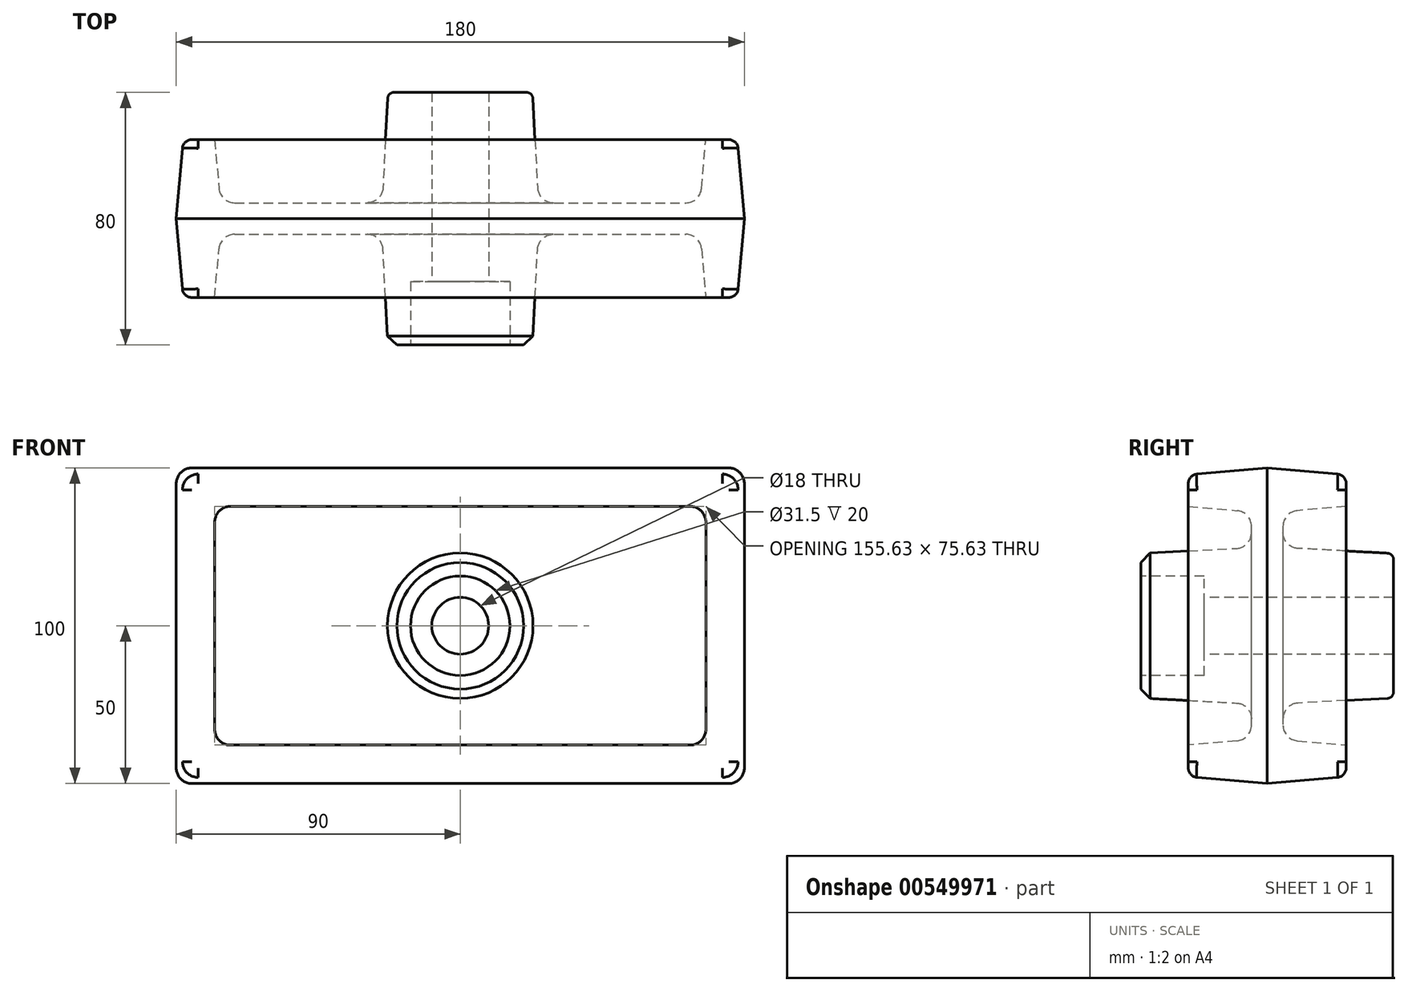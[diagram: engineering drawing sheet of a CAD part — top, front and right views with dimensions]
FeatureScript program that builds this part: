
annotation { "Feature Type Name" : "Feature", "Feature Type Description" : "" }
export const myFeature = defineFeature(function(context is Context, id is Id, definition is map)
    precondition{}
    {
        {
            var Q0;
            Q0=qCreatedBy(makeId("Front.planeOp"),FACE);
            var sketch = newSketch(context, id + "F0", { "sketchPlane" : qUnion([Q0])});
            skLineSegment(sketch, "E0.bottom", {"start": v(90, -50) * mm, "end": v(-90, -50) * mm});
            skLineSegment(sketch, "E0.top", {"start": v(90, 50) * mm, "end": v(-90, 50) * mm});
            skLineSegment(sketch, "E0.left", {"start": v(90, -50) * mm, "end": v(90, 50) * mm});
            skLineSegment(sketch, "E0.right", {"start": v(-90, -50) * mm, "end": v(-90, 50) * mm});
            skPoint(sketch, "E0.middle", {"position": v(0, 0) * mm});
            skSolve(sketch);
        }
        {
            var Q0;
            Q0 = qSketchRegion(id + "F0", true);
            extrude(context, id + "F1", {"entities" : qUnion([Q0]), "depth" : 25 * mm, "offsetDistance" : 25 * mm, "hasDraft" : true, "draftAngle" : 5 * degree, "draftPullDirection" : true, "hasSecondDirection" : true, "secondDirectionOppositeDirection" : true, "secondDirectionDepth" : 25 * mm, "hasSecondDirectionDraft" : true, "secondDirectionDraftAngle" : 5 * degree, "secondDirectionDraftPullDirection" : true});
        }
        {
            var Q0;
            Q0=makeQuery(id+"F1.opExtrude","CAP_FACE",FACE,{"disambiguationData":[OSD([sQuery(id+"F0.wireOp",EDGE,"E0.bottom"),sQuery(id+"F0.wireOp",EDGE,"E0.top"),sQuery(id+"F0.wireOp",EDGE,"E0.left"),sQuery(id+"F0.wireOp",EDGE,"E0.right")])],"isStart":false});
            var sketch = newSketch(context, id + "F2", { "sketchPlane" : qUnion([Q0])});
            skLineSegment(sketch, "E1.0", {"start": v(77.81, -37.81) * mm, "end": v(-77.81, -37.81) * mm});
            skLineSegment(sketch, "E1.1", {"start": v(77.81, -37.81) * mm, "end": v(77.81, 37.81) * mm});
            skLineSegment(sketch, "E1.2", {"start": v(77.81, 37.81) * mm, "end": v(-77.81, 37.81) * mm});
            skLineSegment(sketch, "E1.3", {"start": v(-77.81, -37.81) * mm, "end": v(-77.81, 37.81) * mm});
            skSolve(sketch);
        }
        {
            var Q0;
            Q0 = qSketchRegion(id + "F2", true);
            extrude(context, id + "F3", {"entities" : qUnion([Q0]), "operationType" : NewBodyOperationType.REMOVE, "oppositeDirection" : true, "depth" : 20 * mm, "offsetDistance" : 25 * mm, "hasDraft" : true, "draftAngle" : 5 * degree, "draftPullDirection" : true});
        }
        {
            var Q0;
            Q0=makeQuery(id+"F1.opExtrude","CAP_FACE",FACE,{"disambiguationData":[OSD([sQuery(id+"F0.wireOp",EDGE,"E0.bottom"),sQuery(id+"F0.wireOp",EDGE,"E0.top"),sQuery(id+"F0.wireOp",EDGE,"E0.left"),sQuery(id+"F0.wireOp",EDGE,"E0.right")])],"isStart":true});
            var sketch = newSketch(context, id + "F4", { "sketchPlane" : qUnion([Q0])});
            skLineSegment(sketch, "E2.0", {"start": v(-77.81, 37.81) * mm, "end": v(77.81, 37.81) * mm});
            skLineSegment(sketch, "E2.1", {"start": v(-77.81, -37.81) * mm, "end": v(-77.81, 37.81) * mm});
            skLineSegment(sketch, "E2.2", {"start": v(-77.81, -37.81) * mm, "end": v(77.81, -37.81) * mm});
            skLineSegment(sketch, "E2.3", {"start": v(77.81, -37.81) * mm, "end": v(77.81, 37.81) * mm});
            skSolve(sketch);
        }
        {
            var Q0;
            Q0 = qSketchRegion(id + "F4", true);
            extrude(context, id + "F5", {"entities" : qUnion([Q0]), "operationType" : NewBodyOperationType.REMOVE, "oppositeDirection" : true, "depth" : 20 * mm, "offsetDistance" : 25 * mm, "hasDraft" : true, "draftAngle" : 5 * degree, "draftPullDirection" : true});
        }
        {
            var Q0;
            Q0=makeQuery(id+"F5.boolean.opBoolean","COPY",EDGE,{"derivedFrom":makeQuery(id+"F5.opExtrude","SWEPT_EDGE",EDGE,{"disambiguationData":[OSD([sQuery(id+"F4.wireOp",EDGE,"E2.1"),sQuery(id+"F4.wireOp",EDGE,"E2.2")])]})});
            var Q1;
            Q1=makeQuery(id+"F3.boolean.opBoolean","COPY",EDGE,{"derivedFrom":makeQuery(id+"F3.opExtrude","SWEPT_EDGE",EDGE,{"disambiguationData":[OSD([sQuery(id+"F2.wireOp",EDGE,"E1.0"),sQuery(id+"F2.wireOp",EDGE,"E1.1")])]})});
            var Q2;
            Q2=makeQuery(id+"F3.boolean.opBoolean","COPY",EDGE,{"derivedFrom":makeQuery(id+"F3.opExtrude","SWEPT_EDGE",EDGE,{"disambiguationData":[OSD([sQuery(id+"F2.wireOp",EDGE,"E1.2"),sQuery(id+"F2.wireOp",EDGE,"E1.3")])]})});
            var Q3;
            Q3=makeQuery(id+"F5.boolean.opBoolean","COPY",EDGE,{"derivedFrom":makeQuery(id+"F5.opExtrude","SWEPT_EDGE",EDGE,{"disambiguationData":[OSD([sQuery(id+"F4.wireOp",EDGE,"E2.2"),sQuery(id+"F4.wireOp",EDGE,"E2.3")])]})});
            var Q4;
            Q4=makeQuery(id+"F5.boolean.opBoolean","COPY",EDGE,{"derivedFrom":makeQuery(id+"F5.opExtrude","SWEPT_EDGE",EDGE,{"disambiguationData":[OSD([sQuery(id+"F4.wireOp",EDGE,"E2.0"),sQuery(id+"F4.wireOp",EDGE,"E2.3")])]})});
            var Q5;
            Q5=makeQuery(id+"F5.boolean.opBoolean","COPY",EDGE,{"derivedFrom":makeQuery(id+"F5.opExtrude","SWEPT_EDGE",EDGE,{"disambiguationData":[OSD([sQuery(id+"F4.wireOp",EDGE,"E2.0"),sQuery(id+"F4.wireOp",EDGE,"E2.1")])]})});
            var Q6;
            Q6=makeQuery(id+"F3.boolean.opBoolean","COPY",EDGE,{"derivedFrom":makeQuery(id+"F3.opExtrude","SWEPT_EDGE",EDGE,{"disambiguationData":[OSD([sQuery(id+"F2.wireOp",EDGE,"E1.0"),sQuery(id+"F2.wireOp",EDGE,"E1.3")])]})});
            var Q7;
            Q7=makeQuery(id+"F3.boolean.opBoolean","COPY",EDGE,{"derivedFrom":makeQuery(id+"F3.opExtrude","SWEPT_EDGE",EDGE,{"disambiguationData":[OSD([sQuery(id+"F2.wireOp",EDGE,"E1.1"),sQuery(id+"F2.wireOp",EDGE,"E1.2")])]})});
            fillet(context, id + "F6", {"entities" : qUnion([Q0, Q1, Q2, Q3, Q4, Q5, Q6, Q7]), "radius" : 5 * mm, "allowEdgeOverflow" : false});
        }
        {
            var Q0;
            Q0=makeQuery(id+"F3.boolean.opBoolean","COPY",EDGE,{"derivedFrom":makeQuery(id+"F3.opExtrude","CAP_EDGE",EDGE,{"disambiguationData":[OSD([sQuery(id+"F2.wireOp",EDGE,"E1.0")])],"isStart":false})});
            var Q1;
            Q1=makeQuery(id+"F5.boolean.opBoolean","COPY",EDGE,{"derivedFrom":makeQuery(id+"F5.opExtrude","CAP_EDGE",EDGE,{"disambiguationData":[OSD([sQuery(id+"F4.wireOp",EDGE,"E2.2")])],"isStart":false})});
            fillet(context, id + "F7", {"entities" : qUnion([Q0, Q1]), "radius" : 5 * mm, "tangentPropagation" : true, "allowEdgeOverflow" : false});
        }
        {
            var Q0;
            Q0=makeQuery(id+"F1.*.split.splitOp","SPLIT",EDGE,{"derivedFrom":makeQuery(id+"F1.opExtrude","SWEPT_EDGE",EDGE,{"disambiguationData":[OSD([sQuery(id+"F0.wireOp",EDGE,"E0.bottom"),sQuery(id+"F0.wireOp",EDGE,"E0.right")])]}),"isFromBackBody":true});
            var Q1;
            Q1=makeQuery(id+"F1.*.split.splitOp","SPLIT",EDGE,{"derivedFrom":makeQuery(id+"F1.opExtrude","SWEPT_EDGE",EDGE,{"disambiguationData":[OSD([sQuery(id+"F0.wireOp",EDGE,"E0.top"),sQuery(id+"F0.wireOp",EDGE,"E0.left")])]})});
            var Q2;
            Q2=makeQuery(id+"F1.*.split.splitOp","SPLIT",EDGE,{"derivedFrom":makeQuery(id+"F1.opExtrude","SWEPT_EDGE",EDGE,{"disambiguationData":[OSD([sQuery(id+"F0.wireOp",EDGE,"E0.top"),sQuery(id+"F0.wireOp",EDGE,"E0.left")])]}),"isFromBackBody":true});
            var Q3;
            Q3=makeQuery(id+"F1.*.split.splitOp","SPLIT",EDGE,{"derivedFrom":makeQuery(id+"F1.opExtrude","SWEPT_EDGE",EDGE,{"disambiguationData":[OSD([sQuery(id+"F0.wireOp",EDGE,"E0.top"),sQuery(id+"F0.wireOp",EDGE,"E0.right")])]}),"isFromBackBody":true});
            var Q4;
            Q4=makeQuery(id+"F1.*.split.splitOp","SPLIT",EDGE,{"derivedFrom":makeQuery(id+"F1.opExtrude","SWEPT_EDGE",EDGE,{"disambiguationData":[OSD([sQuery(id+"F0.wireOp",EDGE,"E0.top"),sQuery(id+"F0.wireOp",EDGE,"E0.right")])]})});
            var Q5;
            Q5=makeQuery(id+"F1.*.split.splitOp","SPLIT",EDGE,{"derivedFrom":makeQuery(id+"F1.opExtrude","SWEPT_EDGE",EDGE,{"disambiguationData":[OSD([sQuery(id+"F0.wireOp",EDGE,"E0.bottom"),sQuery(id+"F0.wireOp",EDGE,"E0.left")])]}),"isFromBackBody":true});
            var Q6;
            Q6=makeQuery(id+"F1.*.split.splitOp","SPLIT",EDGE,{"derivedFrom":makeQuery(id+"F1.opExtrude","SWEPT_EDGE",EDGE,{"disambiguationData":[OSD([sQuery(id+"F0.wireOp",EDGE,"E0.bottom"),sQuery(id+"F0.wireOp",EDGE,"E0.right")])]})});
            var Q7;
            Q7=makeQuery(id+"F1.*.split.splitOp","SPLIT",EDGE,{"derivedFrom":makeQuery(id+"F1.opExtrude","SWEPT_EDGE",EDGE,{"disambiguationData":[OSD([sQuery(id+"F0.wireOp",EDGE,"E0.bottom"),sQuery(id+"F0.wireOp",EDGE,"E0.left")])]})});
            fillet(context, id + "F8", {"entities" : qUnion([Q0, Q1, Q2, Q3, Q4, Q5, Q6, Q7]), "radius" : 5 * mm, "tangentPropagation" : true, "allowEdgeOverflow" : false});
        }
        {
            var Q0;
            Q0=makeQuery(id+"F1.opExtrude","CAP_EDGE",EDGE,{"disambiguationData":[OSD([sQuery(id+"F0.wireOp",EDGE,"E0.top")])],"isStart":false});
            var Q1;
            Q1=makeQuery(id+"F1.opExtrude","CAP_EDGE",EDGE,{"disambiguationData":[OSD([sQuery(id+"F0.wireOp",EDGE,"E0.top")])],"isStart":true});
            var Q2;
            Q2=makeQuery(id+"F5.boolean.opBoolean","COPY",EDGE,{"derivedFrom":makeQuery(id+"F5.opExtrude","CAP_EDGE",EDGE,{"disambiguationData":[OSD([sQuery(id+"F4.wireOp",EDGE,"E2.0")])],"isStart":true})});
            var Q3;
            Q3=makeQuery(id+"F3.boolean.opBoolean","COPY",EDGE,{"derivedFrom":makeQuery(id+"F3.opExtrude","CAP_EDGE",EDGE,{"disambiguationData":[OSD([sQuery(id+"F2.wireOp",EDGE,"E1.2")])],"isStart":true})});
            fillet(context, id + "F9", {"entities" : qUnion([Q0, Q1, Q2, Q3]), "radius" : 3 * mm, "tangentPropagation" : true, "allowEdgeOverflow" : false});
        }
        {
            var Q0;
            Q0=qCreatedBy(makeId("Front.planeOp"),FACE);
            var sketch = newSketch(context, id + "F10", { "sketchPlane" : qUnion([Q0])});
            skCircle(sketch, "E3", {"center": v(0, 0) * mm, "radius": 25 * mm});
            skSolve(sketch);
        }
        {
            var Q0;
            Q0 = qSketchRegion(id + "F10", true);
            extrude(context, id + "F11", {"entities" : qUnion([Q0]), "operationType" : NewBodyOperationType.ADD, "endBound" : BoundingType.SYMMETRIC, "depth" : 80 * mm, "offsetDistance" : 25 * mm, "hasDraft" : true, "draftAngle" : 3 * degree, "draftPullDirection" : true});
        }
        {
            var Q0;
            Q0=makeQuery(id+"F11.opExtrude","CAP_FACE",FACE,{"disambiguationData":[OSD([sQuery(id+"F10.wireOp",EDGE,"E3")])],"isStart":false});
            var sketch = newSketch(context, id + "F12", { "sketchPlane" : qUnion([Q0])});
            skPoint(sketch, "E4", {"position": v(0, 0) * mm});
            skPoint(sketch, "E5", {"position": v(-111.25, 156.26) * mm});
            skSolve(sketch);
        }
        {
            var Q0;
            Q0=sQuery(id+"F12.wireOp",VERTEX,"E4");
            var Q1;
            Q1=makeQuery(id+"F1.*.split.splitOp","SPLIT",BODY,{"derivedFrom":makeQuery(id+"F1.opExtrude","SWEPT_BODY",BODY,{"disambiguationData":[OSD([sQuery(id+"F0.wireOp",EDGE,"E0.bottom"),sQuery(id+"F0.wireOp",EDGE,"E0.top"),sQuery(id+"F0.wireOp",EDGE,"E0.left"),sQuery(id+"F0.wireOp",EDGE,"E0.right")])]})});
            hole(context, id + "F13", {"style" : HoleStyle.C_BORE, "endStyle" : HoleEndStyle.THROUGH, "standardTappedOrClearance" : lookupTablePath({ "standard" : "ISO", "fit" : "Normal", "engagement" : "75%", "pitch" : "2 mm", "size" : "M20", "type" : "Tapped" }), "standardBlindInLast" : lookupTablePath({ "fit" : "Standard", "standard" : "ISO", "engagement" : "75%", "pitch" : "2 mm", "size" : "M20", "type" : "Tapped" }), "holeDiameter" : 18 * mm, "cBoreDiameter" : 31.5 * mm, "cBoreDepth" : 20 * mm, "showTappedDepth" : true, "isTappedThrough" : true, "tappedDepth" : 12 * mm, "tapClearance" : 3, "locations" : qUnion([Q0]), "scope" : qUnion([Q1]), "majorDiameter" : 20 * mm});
        }
        {
            var Q0;
            Q0=makeQuery(id+"F11.boolean.opBoolean","INTERSECT",EDGE,{"derivedFrom":[makeQuery(id+"F3.boolean.opBoolean","COPY",FACE,{"derivedFrom":makeQuery(id+"F3.opExtrude","CAP_FACE",FACE,{"disambiguationData":[OSD([sQuery(id+"F2.wireOp",EDGE,"E1.0"),sQuery(id+"F2.wireOp",EDGE,"E1.1"),sQuery(id+"F2.wireOp",EDGE,"E1.2"),sQuery(id+"F2.wireOp",EDGE,"E1.3")])],"isStart":false})}),makeQuery(id+"F11.*.split.splitOp","SPLIT",FACE,{"derivedFrom":makeQuery(id+"F11.opExtrude","SWEPT_FACE",FACE,{"disambiguationData":[OSD([sQuery(id+"F10.wireOp",EDGE,"E3")])]})})]});
            var Q1;
            Q1=makeQuery(id+"F11.boolean.opBoolean","INTERSECT",EDGE,{"derivedFrom":[makeQuery(id+"F5.boolean.opBoolean","COPY",FACE,{"derivedFrom":makeQuery(id+"F5.opExtrude","CAP_FACE",FACE,{"disambiguationData":[OSD([sQuery(id+"F4.wireOp",EDGE,"E2.0"),sQuery(id+"F4.wireOp",EDGE,"E2.1"),sQuery(id+"F4.wireOp",EDGE,"E2.2"),sQuery(id+"F4.wireOp",EDGE,"E2.3")])],"isStart":false})}),makeQuery(id+"F11.*.split.splitOp","SPLIT",FACE,{"derivedFrom":makeQuery(id+"F11.opExtrude","SWEPT_FACE",FACE,{"disambiguationData":[OSD([sQuery(id+"F10.wireOp",EDGE,"E3")])]}),"isFromBackBody":true})]});
            fillet(context, id + "F14", {"entities" : qUnion([Q0, Q1]), "radius" : 5 * mm, "tangentPropagation" : true, "allowEdgeOverflow" : false});
        }
        {
            var Q0;
            Q0=makeQuery(id+"F11.opExtrude","CAP_EDGE",EDGE,{"disambiguationData":[OSD([sQuery(id+"F10.wireOp",EDGE,"E3")])],"isStart":false});
            chamfer(context, id + "F15", {"entities" : qUnion([Q0]), "width" : 3 * mm, "tangentPropagation" : true});
        }
        {
            var Q0;
            Q0=makeQuery(id+"F11.opExtrude","CAP_EDGE",EDGE,{"disambiguationData":[OSD([sQuery(id+"F10.wireOp",EDGE,"E3")])],"isStart":true});
            fillet(context, id + "F16", {"entities" : qUnion([Q0]), "radius" : 2 * mm, "tangentPropagation" : true, "allowEdgeOverflow" : false});
        }
    });
